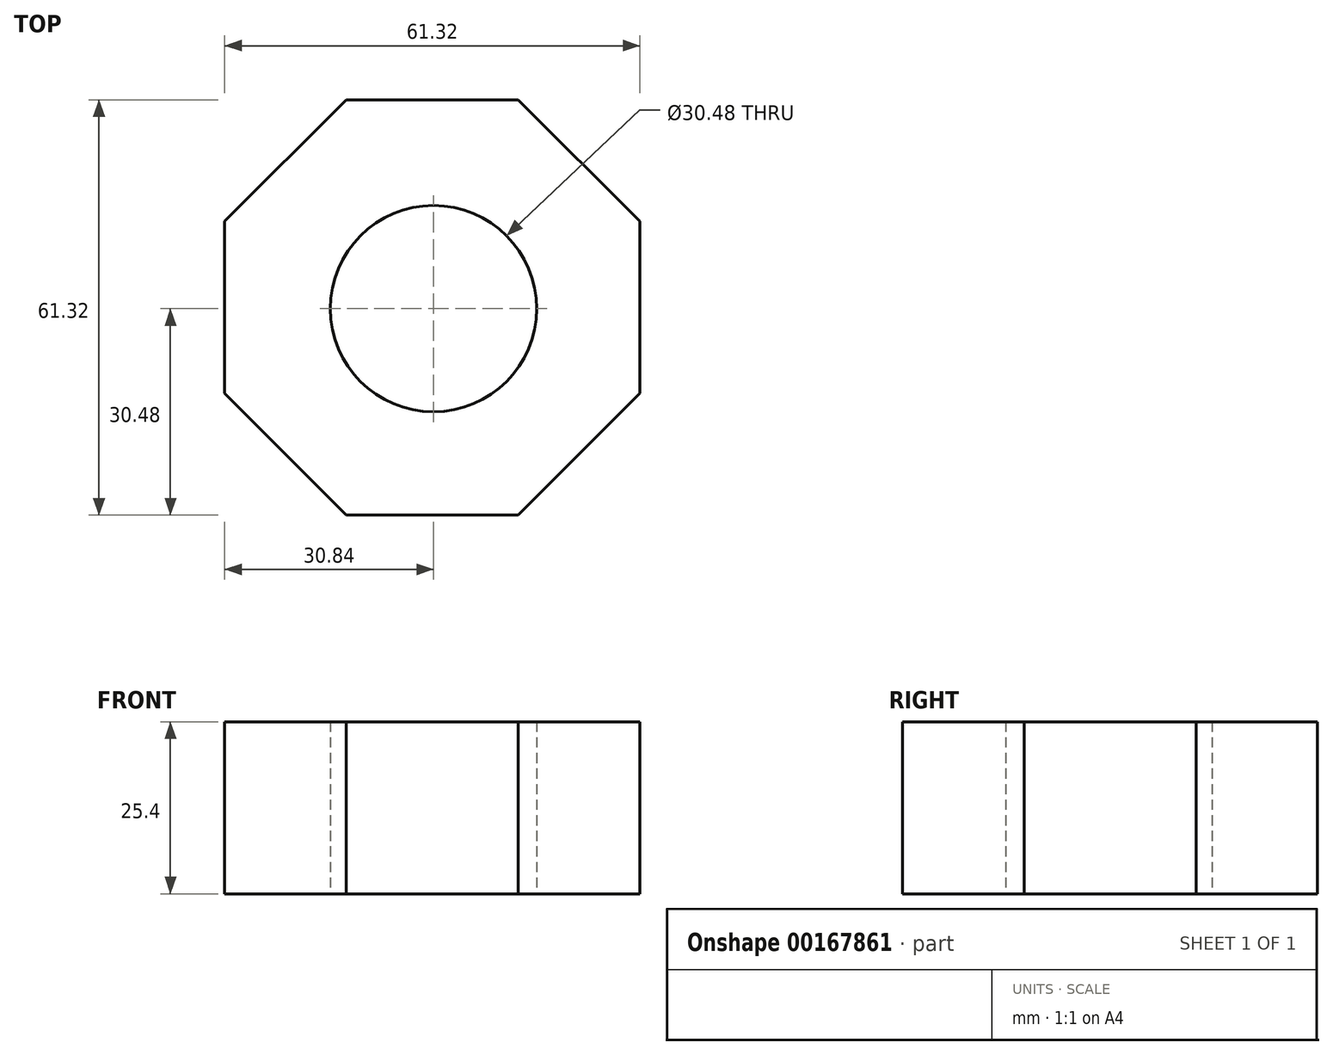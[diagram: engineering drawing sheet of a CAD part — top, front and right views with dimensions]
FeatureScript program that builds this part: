
annotation { "Feature Type Name" : "Feature", "Feature Type Description" : "" }
export const myFeature = defineFeature(function(context is Context, id is Id, definition is map)
    precondition{}
    {
        {
            var Q0;
            Q0=qCreatedBy(makeId("Top.planeOp"),FACE);
            var sketch = newSketch(context, id + "F0", { "sketchPlane" : qUnion([Q0])});
            skLineSegment(sketch, "E0", {"start": v(-12.88, 30.84) * mm, "end": v(12.52, 30.84) * mm});
            skLineSegment(sketch, "E1", {"start": v(12.52, 30.84) * mm, "end": v(30.48, 12.88) * mm});
            skLineSegment(sketch, "E2", {"start": v(30.48, 12.88) * mm, "end": v(30.48, -12.52) * mm});
            skLineSegment(sketch, "E3", {"start": v(30.48, -12.52) * mm, "end": v(12.52, -30.48) * mm});
            skLineSegment(sketch, "E4", {"start": v(12.52, -30.48) * mm, "end": v(-12.88, -30.48) * mm});
            skLineSegment(sketch, "E5", {"start": v(-12.88, -30.48) * mm, "end": v(-30.84, -12.52) * mm});
            skLineSegment(sketch, "E6", {"start": v(-30.84, -12.52) * mm, "end": v(-30.84, 12.88) * mm});
            skLineSegment(sketch, "E7", {"start": v(-30.84, 12.88) * mm, "end": v(-12.88, 30.84) * mm});
            skCircle(sketch, "E8", {"center": v(0, 0) * mm, "radius": 15.24 * mm});
            skSolve(sketch);
        }
        {
            var Q0;
            Q0 = qSketchRegion(id + "F0", true);
            extrude(context, id + "F1", {"entities" : qUnion([Q0]), "depth" : 25.4 * mm});
        }
    });
